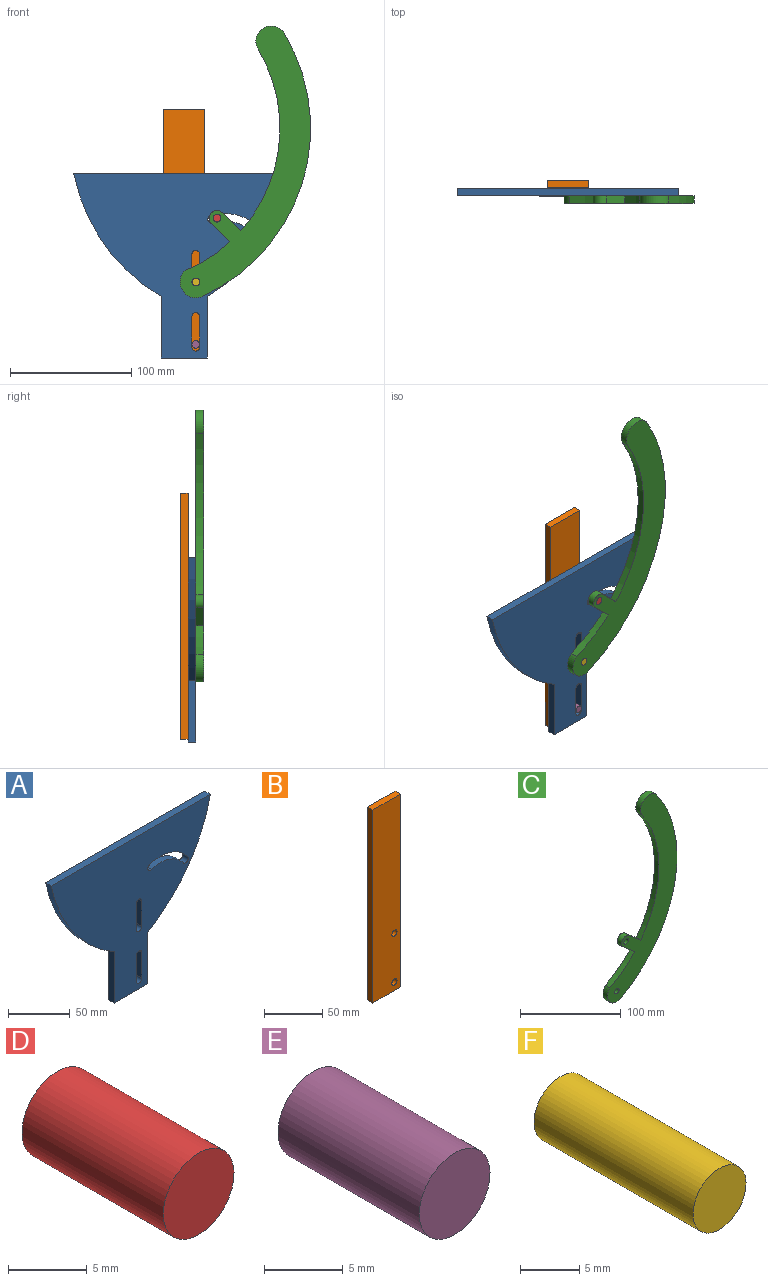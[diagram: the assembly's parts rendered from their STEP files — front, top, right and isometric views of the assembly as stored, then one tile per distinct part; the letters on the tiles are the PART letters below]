
ASSEMBLY  parts=6 mates=8
PART A: 20 faces, bbox 182.5x6.4x152.4 mm
  f0: plane 182.51x152.4mm, normal (0,1,0), area 14674.7mm2, adj f2,f3,f4,f5,f6,f7,f8,f9
  f1: plane 182.51x152.4mm, normal (0,-1,0), area 14674.7mm2, adj f2,f3,f4,f5,f6,f7,f8,f9
  f2: plane 38.1x6.35mm, normal (0,0,-1), area 241.9mm2, adj f0,f1,f3,f7
  f3: plane 50.8x6.35mm, normal (1,0,0), area 322.6mm2, adj f0,f1,f2,f4
  f4: cylinder r=152.4mm len=101.6mm, axis (0,-1,0), area 815.4mm2, adj f0,f1,f3,f5
  f5: plane 182.51x6.35mm, normal (0,0,1), area 1159mm2, adj f0,f1,f4,f6
  f6: cylinder r=152.4mm len=101.6mm, axis (0,-1,0), area 815.4mm2, adj f0,f1,f5,f7
  f7: plane 50.8x6.35mm, normal (-1,0,0), area 322.6mm2, adj f0,f1,f2,f6
  f8: plane 25.4x6.35mm, normal (-1,0,0), area 161.3mm2, adj f0,f1,f9,f11
  f9: cylinder r=3.17mm len=6.35mm, axis (0,-1,0), area 63.3mm2, adj f0,f1,f8,f10
  f10: plane 25.4x6.35mm, normal (1,0,0), area 161.3mm2, adj f0,f1,f9,f11
  f11: cylinder r=3.17mm len=6.35mm, axis (0,-1,0), area 63.3mm2, adj f0,f1,f8,f10
  f12: cylinder r=3.17mm len=6.35mm, axis (0,-1,0), area 63.3mm2, adj f0,f1,f13,f15
  f13: plane 25.4x6.35mm, normal (-1,0,0), area 161.3mm2, adj f0,f1,f12,f14
  f14: cylinder r=3.17mm len=6.35mm, axis (0,-1,0), area 63.3mm2, adj f0,f1,f13,f15
  f15: plane 25.4x6.35mm, normal (1,0,0), area 161.3mm2, adj f0,f1,f12,f14
  f16: cylinder r=3.17mm len=6.35mm, axis (0,1,0), area 63.3mm2, adj f0,f1,f17,f19
  f17: cylinder r=39.2mm len=43.62mm, axis (0,1,0), area 310.3mm2, adj f0,f1,f16,f18
  f18: cylinder r=3.17mm len=6.35mm, axis (0,1,0), area 63.3mm2, adj f0,f1,f17,f19
  f19: cylinder r=32.85mm len=36.56mm, axis (0,1,0), area 260mm2, adj f0,f1,f16,f18
PART B: 8 faces, bbox 34x6.4x203.2 mm
  f0: plane 203.2x6.35mm, normal (1,0,0), area 1290.3mm2, adj f1,f5,f6,f7
  f1: plane 34.04x6.35mm, normal (0,0,1), area 216.1mm2, adj f0,f2,f6,f7
  f2: plane 203.2x6.35mm, normal (-1,0,0), area 1290.3mm2, adj f1,f5,f6,f7
  f3: cylinder r=3.17mm len=6.35mm, axis (0,1,0), area 126.7mm2, adj f6,f7
  f4: cylinder r=3.17mm len=6.35mm, axis (0,1,0), area 126.7mm2, adj f6,f7
  f5: plane 34.04x6.35mm, normal (0,0,-1), area 216.1mm2, adj f0,f2,f6,f7
  f6: plane 203.2x34.04mm, normal (0,-1,0), area 6852.8mm2, adj f0,f1,f2,f3,f4,f5
  f7: plane 203.2x34.04mm, normal (0,1,0), area 6852.8mm2, adj f0,f1,f2,f3,f4,f5
PART C: 12 faces, bbox 97.7x6.4x228.8 mm
  f0: cylinder r=127.11mm len=34.96mm, axis (0,1,0), area 280.1mm2, adj f1,f8,f10,f11
  f1: cylinder r=13mm len=21.84mm, axis (0,1,0), area 233.3mm2, adj f0,f2,f10,f11
  f2: cylinder r=152.4mm len=221.92mm, axis (0,1,0), area 1630.5mm2, adj f1,f3,f10,f11
  f3: cylinder r=12.65mm len=22.93mm, axis (0,1,0), area 252.3mm2, adj f2,f4,f10,f11
  f4: cylinder r=127.11mm len=150.73mm, axis (0,1,0), area 1024.7mm2, adj f3,f5,f10,f11
  f5: plane 16.37x13.74mm, normal (0.64,0,0.77), area 135.7mm2, adj f4,f6,f10,f11
  f6: cylinder r=6.35mm len=11.21mm, axis (0,1,0), area 126.7mm2, adj f5,f8,f10,f11
  f7: cylinder r=3.17mm len=6.35mm, axis (0,1,0), area 126.7mm2, adj f10,f11
  f8: plane 16.37x13.74mm, normal (-0.64,0,-0.77), area 135.7mm2, adj f0,f6,f10,f11
  f9: cylinder r=3.17mm len=6.35mm, axis (0,1,0), area 126.7mm2, adj f10,f11
  f10: plane 228.84x97.66mm, normal (0,-1,0), area 6742.7mm2, adj f0,f1,f2,f3,f4,f5,f6,f7
  f11: plane 228.84x97.66mm, normal (0,1,0), area 6742.7mm2, adj f0,f1,f2,f3,f4,f5,f6,f7
PART D: 3 faces, bbox 6.4x12.7x6.4 mm
  f0: cylinder r=3.17mm len=12.7mm, axis (0,-1,0), area 253.4mm2, adj f1,f2
  f1: plane 6.35x6.35mm, normal (0,1,0), area 31.7mm2, adj f0
  f2: plane 6.35x6.35mm, normal (0,-1,0), area 31.7mm2, adj f0
PART E: 3 faces, bbox 6.4x12.7x6.4 mm
  f0: cylinder r=3.17mm len=12.7mm, axis (0,-1,0), area 253.4mm2, adj f1,f2
  f1: plane 6.35x6.35mm, normal (0,1,0), area 31.7mm2, adj f0
  f2: plane 6.35x6.35mm, normal (0,-1,0), area 31.7mm2, adj f0
PART F: 3 faces, bbox 6.4x19.1x6.4 mm
  f0: cylinder r=3.17mm len=19.05mm, axis (0,-1,0), area 380mm2, adj f1,f2
  f1: plane 6.35x6.35mm, normal (0,1,0), area 31.7mm2, adj f0
  f2: plane 6.35x6.35mm, normal (0,-1,0), area 31.7mm2, adj f0
PLACE A at identity
PLACE B t=(0,12.7,2.38)mm
PLACE C rot(axis=(0,1,0),4.7deg) t=(-4.88,6.35,3.36)mm
PLACE D rot(axis=(-1,0,0.04),180deg) t=(13.74,0,231.2)mm
PLACE E t=(0,6.35,2.38)mm
PLACE F t=(0,6.35,2.38)mm
MATE planar C.f11 <-> A.f1  axis (0,1,0) through (66.43,0,151.74)mm
MATE cylindrical F.f0 <-> C.f1  axis (0,-1,0) through (9.53,-6.35,62.71)mm
MATE parallel B.f2 <-> A.f7  axis (-1,0,0) through (-17.02,9.52,103.98)mm
MATE planar A.f0 <-> B.f6  axis (0,1,0) through (-19.05,6.35,25.4)mm
MATE fastened F.f0 <-> B.f3  axis (0,1,0) through (9.53,12.7,62.71)mm
MATE fastened D.f0 <-> C.f6  axis (0,-1,0) through (27.02,-6.35,115.43)mm
MATE fastened B.f4 <-> E.f0  axis (0,1,0) through (9.52,12.7,11.27)mm
MATE pin_slot E.f0 <-> A.f11  axis (0,-1,0) through (9.52,0,11.27)mm
